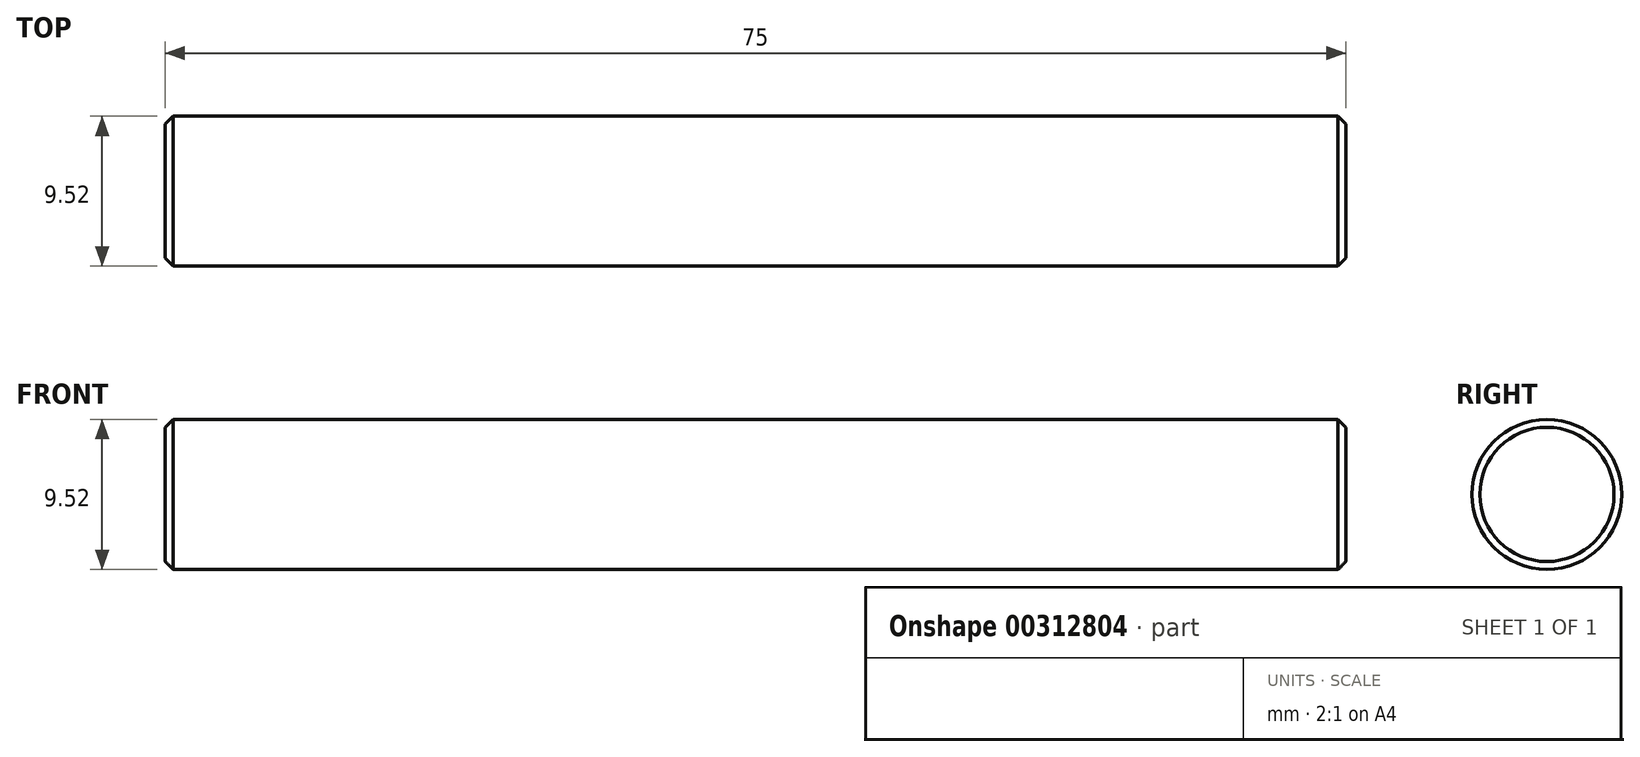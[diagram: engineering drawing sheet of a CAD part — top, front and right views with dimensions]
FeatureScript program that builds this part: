
annotation { "Feature Type Name" : "Feature", "Feature Type Description" : "" }
export const myFeature = defineFeature(function(context is Context, id is Id, definition is map)
    precondition{}
    {
        {
            var Q0;
            Q0=qCreatedBy(makeId("Right.planeOp"),FACE);
            var sketch = newSketch(context, id + "F0", { "sketchPlane" : qUnion([Q0])});
            skCircle(sketch, "E0", {"center": v(0, 0) * mm, "radius": 4.76 * mm});
            skSolve(sketch);
        }
        {
            var Q0;
            Q0=qSketchRegion(id+"F0",true);
            extrude(context, id + "F1", {"entities" : qUnion([Q0]), "depth" : 75 * mm});
        }
        {
            var Q0;
            Q0=makeQuery(id+"F1.opExtrude","CAP_EDGE",EDGE,{"disambiguationData":[OSD([sQuery(id+"F0.wireOp",EDGE,"E0")])],"isStart":false});
            var Q1;
            Q1=makeQuery(id+"F1.opExtrude","CAP_EDGE",EDGE,{"disambiguationData":[OSD([sQuery(id+"F0.wireOp",EDGE,"E0")])],"isStart":true});
            chamfer(context, id + "F2", {"entities" : qUnion([Q0, Q1]), "width" : .5 * mm, "tangentPropagation" : true});
        }
    });
